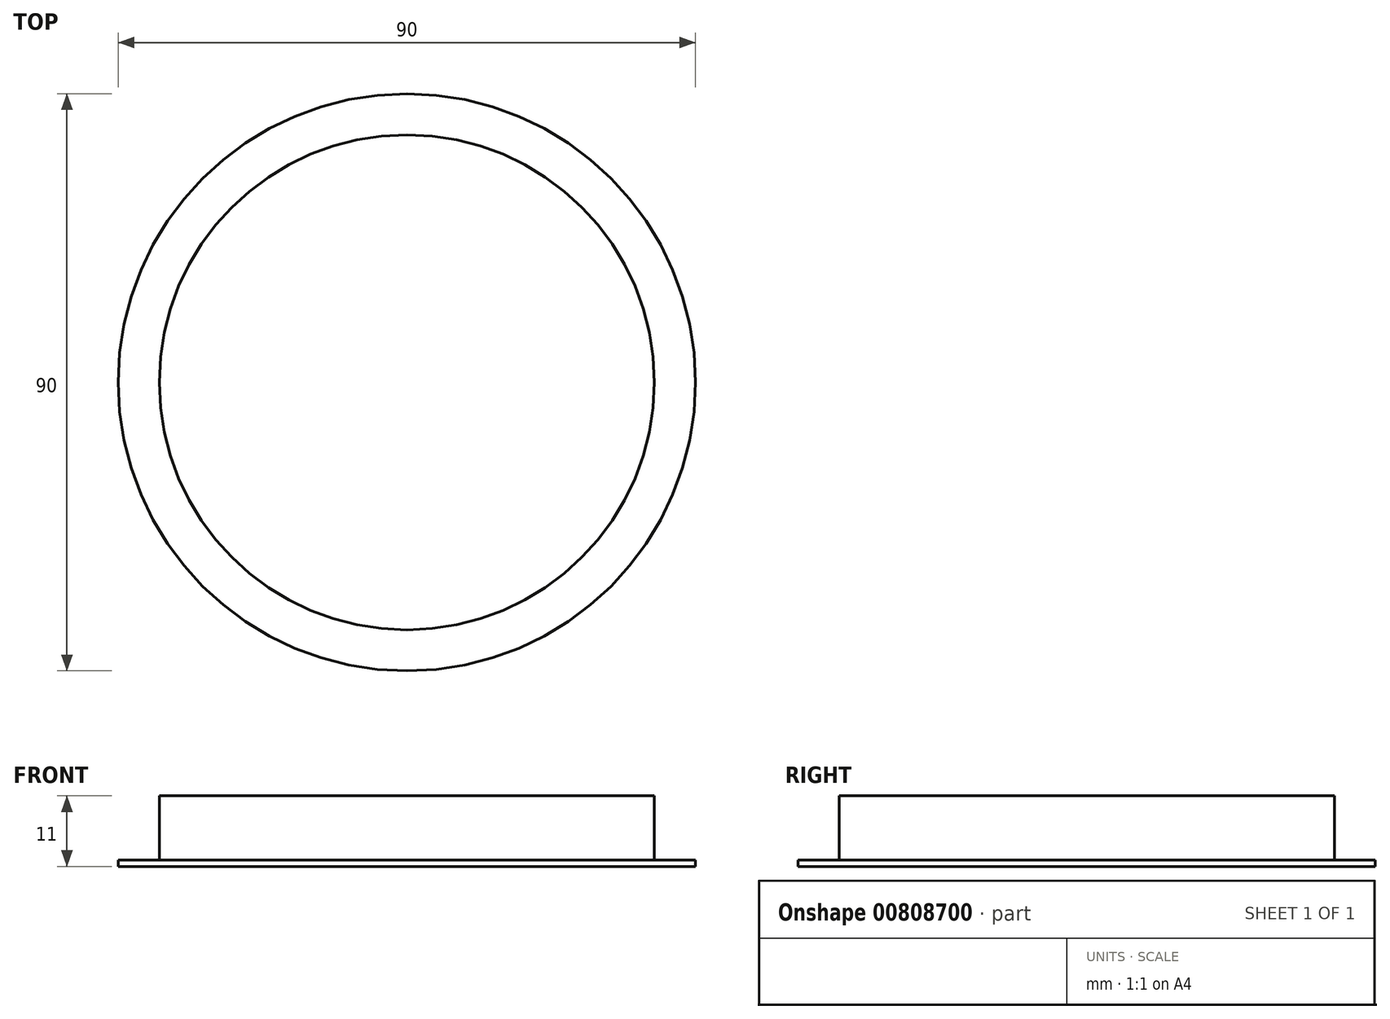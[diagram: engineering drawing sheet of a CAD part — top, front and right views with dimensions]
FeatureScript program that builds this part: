
annotation { "Feature Type Name" : "Feature", "Feature Type Description" : "" }
export const myFeature = defineFeature(function(context is Context, id is Id, definition is map)
    precondition{}
    {
        {
            var Q0;
            Q0=qCreatedBy(makeId("Top.planeOp"),FACE);
            var sketch = newSketch(context, id + "F0", { "sketchPlane" : qUnion([Q0])});
            skCircle(sketch, "E0", {"center": v(0, 0) * mm, "radius": 45 * mm});
            skSolve(sketch);
        }
        {
            var Q0;
            Q0=qSketchRegion(id+"F0",true);
            extrude(context, id + "F1", {"entities" : qUnion([Q0]), "depth" : 1 * mm, "offsetDistance" : 25.4 * mm});
        }
        {
            var Q0;
            Q0=makeQuery(id+"F1.opExtrude","CAP_FACE",FACE,{"disambiguationData":[OSD([sQuery(id+"F0.wireOp",EDGE,"E0")])],"isStart":false});
            var sketch = newSketch(context, id + "F2", { "sketchPlane" : qUnion([Q0])});
            skCircle(sketch, "E1", {"center": v(0, 0) * mm, "radius": 38.6 * mm});
            skSolve(sketch);
        }
        {
            var Q0;
            Q0=makeQuery(id+"F2.imprint","IMPRINT",FACE,{"disambiguationData":[TD([[makeQuery(id+"F2.imprint","IMPRINT",EDGE,{"derivedFrom":sQuery(id+"F2.wireOp",EDGE,"E1")}),1.0]])]});
            extrude(context, id + "F3", {"entities" : qUnion([Q0]), "depth" : 10 * mm, "offsetDistance" : 25.4 * mm});
        }
    });
